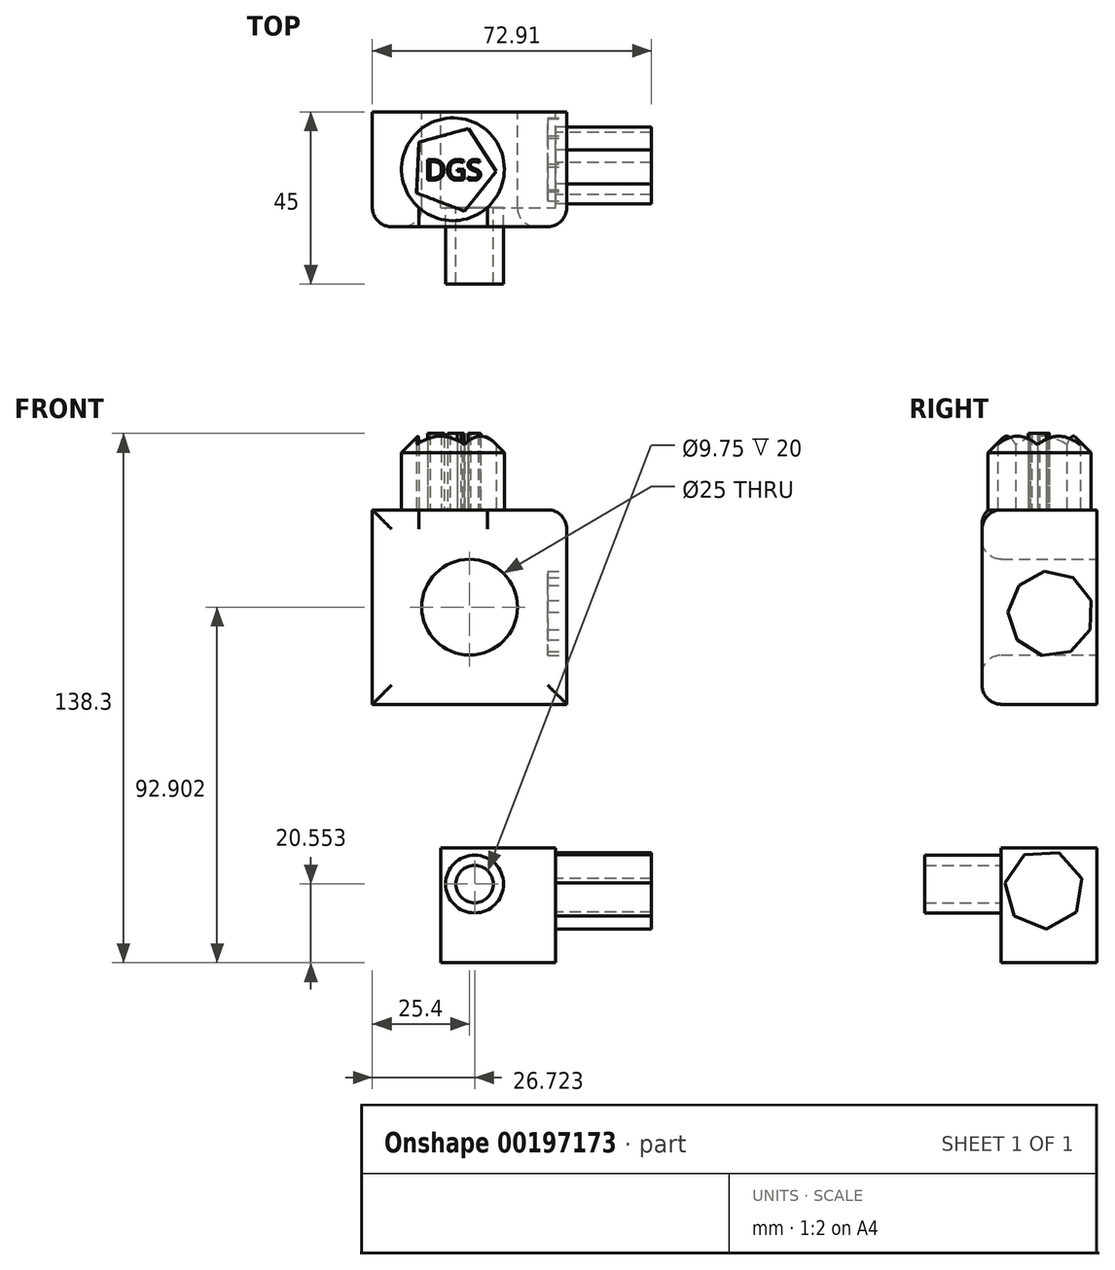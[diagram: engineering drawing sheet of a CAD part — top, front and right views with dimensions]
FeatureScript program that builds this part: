
annotation { "Feature Type Name" : "Feature", "Feature Type Description" : "" }
export const myFeature = defineFeature(function(context is Context, id is Id, definition is map)
    precondition{}
    {
        {
            var Q0;
            Q0=qCreatedBy(makeId("Front.planeOp"),FACE);
            var sketch = newSketch(context, id + "F0", { "sketchPlane" : qUnion([Q0])});
            skLineSegment(sketch, "E0.bottom", {"start": v(-63.96, 67.06) * mm, "end": v(-13.16, 67.06) * mm});
            skLineSegment(sketch, "E0.top", {"start": v(-63.96, 16.26) * mm, "end": v(-13.16, 16.26) * mm});
            skLineSegment(sketch, "E0.left", {"start": v(-63.96, 67.06) * mm, "end": v(-63.96, 16.26) * mm});
            skLineSegment(sketch, "E0.right", {"start": v(-13.16, 67.06) * mm, "end": v(-13.16, 16.26) * mm});
            skCircle(sketch, "E1", {"center": v(-38.56, 41.66) * mm, "radius": 12.5 * mm});
            skSolve(sketch);
        }
        {
            var Q0;
            Q0 = qSketchRegion(id + "F0", true);
            extrude(context, id + "F1", {"entities" : qUnion([Q0]), "depth" : 30 * mm});
        }
        {
            var Q0;
            Q0=makeQuery(id+"F1.opExtrude","SWEPT_FACE",FACE,{"disambiguationData":[OSD([sQuery(id+"F0.wireOp",EDGE,"E0.bottom")])]});
            var sketch = newSketch(context, id + "F2", { "sketchPlane" : qUnion([Q0])});
            skCircle(sketch, "E2", {"center": v(-42.9, -15) * mm, "radius": 13.42 * mm});
            skPoint(sketch, "E2.centerSnap0", {"position": v(-63.96, -15) * mm});
            skCircle(sketch, "E3.cCircle", {"center": v(-42.9, -15) * mm, "radius": 9.17 * mm, "construction": true});
            skLineSegment(sketch, "E3.0", {"start": v(-31.57, -15.54) * mm, "end": v(-39.91, -25.94) * mm});
            skLineSegment(sketch, "E3.1", {"start": v(-39.91, -25.94) * mm, "end": v(-52.38, -21.22) * mm});
            skLineSegment(sketch, "E3.2", {"start": v(-52.38, -21.22) * mm, "end": v(-51.74, -7.9) * mm});
            skLineSegment(sketch, "E3.3", {"start": v(-51.74, -7.9) * mm, "end": v(-38.88, -4.4) * mm});
            skLineSegment(sketch, "E3.4", {"start": v(-38.88, -4.4) * mm, "end": v(-31.57, -15.54) * mm});
            skPoint(sketch, "E3.0.midPoint", {"position": v(-35.74, -20.74) * mm});
            skSolve(sketch);
        }
        {
            var Q0;
            Q0 = qSketchRegion(id + "F2", true);
            extrude(context, id + "F3", {"entities" : qUnion([Q0]), "operationType" : NewBodyOperationType.ADD, "depth" : 20 * mm});
        }
        {
            var Q0;
            Q0=makeQuery(id+"F1.opExtrude","SWEPT_FACE",FACE,{"disambiguationData":[OSD([sQuery(id+"F0.wireOp",EDGE,"E0.right")])]});
            var sketch = newSketch(context, id + "F4", { "sketchPlane" : qUnion([Q0])});
            skCircle(sketch, "E4.cCircle", {"center": v(-12.1, 39.93) * mm, "radius": 10.48 * mm, "construction": true});
            skLineSegment(sketch, "E4.0", {"start": v(-20.4, 47.38) * mm, "end": v(-13.68, 50.97) * mm});
            skLineSegment(sketch, "E4.1", {"start": v(-13.68, 50.97) * mm, "end": v(-6.2, 49.4) * mm});
            skLineSegment(sketch, "E4.2", {"start": v(-6.2, 49.4) * mm, "end": v(-1.5, 43.39) * mm});
            skLineSegment(sketch, "E4.3", {"start": v(-1.5, 43.39) * mm, "end": v(-1.76, 35.76) * mm});
            skLineSegment(sketch, "E4.4", {"start": v(-1.76, 35.76) * mm, "end": v(-6.86, 30.08) * mm});
            skLineSegment(sketch, "E4.5", {"start": v(-6.86, 30.08) * mm, "end": v(-14.41, 29.01) * mm});
            skLineSegment(sketch, "E4.6", {"start": v(-14.41, 29.01) * mm, "end": v(-20.89, 33.05) * mm});
            skLineSegment(sketch, "E4.7", {"start": v(-20.89, 33.05) * mm, "end": v(-23.26, 40.3) * mm});
            skLineSegment(sketch, "E4.8", {"start": v(-23.26, 40.3) * mm, "end": v(-20.4, 47.38) * mm});
            skPoint(sketch, "E4.0.midPoint", {"position": v(-17.04, 49.18) * mm});
            skSolve(sketch);
        }
        {
            var Q0;
            Q0=makeQuery(id+"F4.imprint","IMPRINT",FACE,{"disambiguationData":[TD([[makeQuery(id+"F4.imprint","IMPRINT",EDGE,{"derivedFrom":sQuery(id+"F4.wireOp",EDGE,"E4.0")}),-1.0]])]});
            var Q1;
            Q1=makeQuery(id+"F1.opExtrude","SWEPT_FACE",FACE,{"disambiguationData":[OSD([sQuery(id+"F0.wireOp",EDGE,"E0.left")])]});
            var Q2;
            Q2=makeQuery(id+"F3.opExtrude","CAP_VERTEX",VERTEX,{"disambiguationData":[OSD([sQuery(id+"F2.wireOp",EDGE,"E3.1"),sQuery(id+"F2.wireOp",EDGE,"E3.2")])],"isStart":false});
            extrude(context, id + "F5", {"entities" : qUnion([Q0]), "operationType" : NewBodyOperationType.REMOVE, "oppositeDirection" : true, "endBoundEntityFace" : qUnion([Q1]), "endBoundEntityVertex" : qUnion([Q2]), "depth" : 5 * mm});
        }
        {
            var Q0;
            Q0=makeQuery(id+"F1.opExtrude","SWEPT_EDGE",EDGE,{"disambiguationData":[OSD([sQuery(id+"F0.wireOp",EDGE,"E0.bottom"),sQuery(id+"F0.wireOp",EDGE,"E0.right")])]});
            var Q1;
            Q1=makeQuery(id+"F1.opExtrude","CAP_EDGE",EDGE,{"disambiguationData":[OSD([sQuery(id+"F0.wireOp",EDGE,"E0.right")])],"isStart":false});
            var Q2;
            Q2=makeQuery(id+"F1.opExtrude","CAP_EDGE",EDGE,{"disambiguationData":[OSD([sQuery(id+"F0.wireOp",EDGE,"E0.top")])],"isStart":false});
            var Q3;
            Q3=makeQuery(id+"F1.opExtrude","CAP_FACE",FACE,{"disambiguationData":[OSD([sQuery(id+"F0.wireOp",EDGE,"E0.bottom"),sQuery(id+"F0.wireOp",EDGE,"E0.top"),sQuery(id+"F0.wireOp",EDGE,"E0.left"),sQuery(id+"F0.wireOp",EDGE,"E0.right"),sQuery(id+"F0.wireOp",EDGE,"E1")])],"isStart":false});
            fillet(context, id + "F6", {"entities" : qUnion([Q0, Q1, Q2, Q3]), "radius" : 5 * mm, "tangentPropagation" : true, "allowEdgeOverflow" : false});
        }
        {
            var Q0;
            Q0=makeQuery(id+"F3.opExtrude","CAP_EDGE",EDGE,{"disambiguationData":[OSD([sQuery(id+"F2.wireOp",EDGE,"E2")])],"isStart":false});
            chamfer(context, id + "F7", {"entities" : qUnion([Q0]), "width" : 5 * mm, "tangentPropagation" : true});
        }
        {
            var Q0;
            Q0=makeQuery(id+"F3.boolean.opBoolean","SPLIT",FACE,{"disambiguationData":[TD([makeQuery(id+"F3.opExtrude","SWEPT_FACE",FACE,{"disambiguationData":[OSD([sQuery(id+"F2.wireOp",EDGE,"E3.0")])]})])],"derivedFrom":makeQuery(id+"F1.opExtrude","SWEPT_FACE",FACE,{"disambiguationData":[OSD([sQuery(id+"F0.wireOp",EDGE,"E0.bottom")])]})});
            var sketch = newSketch(context, id + "F8", { "sketchPlane" : qUnion([Q0])});
            skText(sketch, "E5", { "text": "DGS", "fontName": "OpenSans-Regular.ttf"});
            const initialGuessF8  = {"E5": [-0.0502, -0.0178, 1, 0, 0.00534]};
            skSetInitialGuess(sketch, initialGuessF8);
            skSolve(sketch);
        }
        {
            var Q0;
            Q0 = qSketchRegion(id + "F8", true);
            extrude(context, id + "F9", {"entities" : qUnion([Q0]), "operationType" : NewBodyOperationType.ADD, "depth" : 20 * mm});
        }
        {
            var Q0;
            Q0=qCreatedBy(makeId("Front.planeOp"),FACE);
            var sketch = newSketch(context, id + "F10", { "sketchPlane" : qUnion([Q0])});
            skLineSegment(sketch, "E6.bottom", {"start": v(-46.05, -21.24) * mm, "end": v(-16.05, -21.24) * mm});
            skLineSegment(sketch, "E6.top", {"start": v(-46.05, -51.24) * mm, "end": v(-16.05, -51.24) * mm});
            skLineSegment(sketch, "E6.left", {"start": v(-46.05, -21.24) * mm, "end": v(-46.05, -51.24) * mm});
            skLineSegment(sketch, "E6.right", {"start": v(-16.05, -21.24) * mm, "end": v(-16.05, -51.24) * mm});
            skSolve(sketch);
        }
        {
            var Q0;
            Q0=makeQuery(id+"F10.imprint","IMPRINT",FACE,{"disambiguationData":[TD([[makeQuery(id+"F10.imprint","IMPRINT",EDGE,{"derivedFrom":sQuery(id+"F10.wireOp",EDGE,"E6.bottom")}),-1.0]])]});
            extrude(context, id + "F11", {"entities" : qUnion([Q0]), "depth" : 25 * mm});
        }
        {
            var Q0;
            Q0=makeQuery(id+"F11.opExtrude","CAP_FACE",FACE,{"disambiguationData":[OSD([sQuery(id+"F10.wireOp",EDGE,"E6.bottom"),sQuery(id+"F10.wireOp",EDGE,"E6.top"),sQuery(id+"F10.wireOp",EDGE,"E6.left"),sQuery(id+"F10.wireOp",EDGE,"E6.right")])],"isStart":false});
            var sketch = newSketch(context, id + "F12", { "sketchPlane" : qUnion([Q0])});
            skCircle(sketch, "E7", {"center": v(-37.24, -30.69) * mm, "radius": 7.55 * mm});
            skCircle(sketch, "E8", {"center": v(-37.24, -30.69) * mm, "radius": 4.88 * mm});
            skSolve(sketch);
        }
        {
            var Q0;
            Q0 = qSketchRegion(id + "F12", true);
            extrude(context, id + "F13", {"entities" : qUnion([Q0]), "operationType" : NewBodyOperationType.ADD, "depth" : 20 * mm});
        }
        {
            var Q0;
            Q0=makeQuery(id+"F11.opExtrude","SWEPT_FACE",FACE,{"disambiguationData":[OSD([sQuery(id+"F10.wireOp",EDGE,"E6.right")])]});
            var sketch = newSketch(context, id + "F14", { "sketchPlane" : qUnion([Q0])});
            skCircle(sketch, "E9.cCircle", {"center": v(-13.87, -32.07) * mm, "radius": 9.33 * mm, "construction": true});
            skLineSegment(sketch, "E9.0", {"start": v(-5.42, -38.07) * mm, "end": v(-13.29, -42.42) * mm});
            skLineSegment(sketch, "E9.1", {"start": v(-13.29, -42.42) * mm, "end": v(-21.6, -38.98) * mm});
            skLineSegment(sketch, "E9.2", {"start": v(-21.6, -38.98) * mm, "end": v(-24.09, -30.34) * mm});
            skLineSegment(sketch, "E9.3", {"start": v(-24.09, -30.34) * mm, "end": v(-18.89, -23) * mm});
            skLineSegment(sketch, "E9.4", {"start": v(-18.89, -23) * mm, "end": v(-9.9, -22.5) * mm});
            skLineSegment(sketch, "E9.5", {"start": v(-9.9, -22.5) * mm, "end": v(-3.92, -29.2) * mm});
            skLineSegment(sketch, "E9.6", {"start": v(-3.92, -29.2) * mm, "end": v(-5.42, -38.07) * mm});
            skPoint(sketch, "E9.0.midPoint", {"position": v(-9.36, -40.24) * mm});
            skSolve(sketch);
        }
        {
            var Q0;
            Q0 = qSketchRegion(id + "F14", true);
            extrude(context, id + "F15", {"entities" : qUnion([Q0]), "operationType" : NewBodyOperationType.ADD, "depth" : 25 * mm});
        }
    });
